# Revit family: ConcealedCistern-ForWallHungWCPans-8cm-WithAdjustableThinMetalFeet-VitrA-768-1851
name_source: partatom
category: Plumbing Fixtures
revit_build: Autodesk Revit 2017 (Build: 20160225_1515(x64)
units: mm (PartAtom-declared; Revit-internal decimal feet)

## family parameters
Cut with Voids When Loaded = No
Host = Face
OmniClass Number = 23.45.00.00
OmniClass Title = Sanitary, Laundry, and Cleaning Equipment
Part Type = Normal
Room Calculation Point = No
Round Connector Dimension = Use Diameter
Shared = Yes

## types (2) — shared parameters
BIMobject category = Toilet Cisterns
Brand = Vitra
CW Connection = Yes
Coating Material = Console
Default Elevation = 1000 mm  [stored 3.28084 ft]
Design country = Turkey
HW Connection = No
IFC Classification = Sanitary Terminal
Manufacturer = Vitra
Manufacturer name = Vitra
Mounting type = Assembly to floor
NBS Referans Code = 35-93-90
NBS Referans Description = Wc Cisterns
Nominal Depth (mm) = 80 mm  [stored 0.262467 ft]
Nominal Height (mm) = 1100 mm
Nominal Width (mm) = 500 mm  [stored 1.64042 ft]
OmniClass Code = 23-31 19 19
OmniClass Description = Water Closets
Outlet Angle = 45.00°
Primary Material = Orange
Product Type = Concealed Cistern
Product certification = https://www.vitraglobal.com
Product family = Vitra
Product group = Concealed Cistern for Wall-Hung WC Pans
Product url = https://www.vitra.com.tr
Secondary Material = White
Technical description = https://www.vitra.com.tr
Third Material = Blue
URL = https://www.vitra.com.tr
Uniclass 2.0 Code = PR-35-93-90
Uniclass 2.0 Description = Wc Cisterns
Uniclass 2015 Code = Pr_40_20_93_89
Uniclass 2015 Name = WC cisterns
Vent Connection = No
Warranty Period (Year) = 10 Years
Waste Connection = Yes
Weight Net (kg) = 8
Youtube = https://www.youtube.com

## per-type parameters (varying)
| type | Article No. (default) | Description | Model | Product Properties | Product SKU |
| ConcealedCistern-ForWallHungWCPans-3/6lt-WithAdjustableThickMetalFeet-8cm-FloorMounting-VitrA-768-1851-01 | 768-1851-01 | VitrA Concealed Cistern for Wall-Hung WC Pans
Standart Installation Set - Adjusted to 3/6lt - 8 cm | 768-1851-01 | Concealed Cistern for Wall-Hung WC Pans
Standart Installation Set - Adjusted to 3/6lt 8 cm | 768-1851-01 |
| ConcealedCistern-ForWallHungWCPans-2.5/4lt-WithAdjustableThickMetalFeet-8cm-FloorMounting-VitrA-768-1851-02 | 768-1851-02 | VitrA Concealed Cistern for Wall-Hung WC Pans
Standart Installation Set - Adjusted to 2.5/4lt - 8 cm | 768-1851-02 | Concealed Cistern for Wall-Hung WC Pans
Standart Installation Set - Adjusted to 2.5/4lt - 8cm | 768-1851-02 |

note: [stored X ft] marks values corroborated as IEEE doubles in the binary element streams (Revit-internal decimal feet)

## geometry (parser evidence)
native form markers: Sweep x1
no freeform markers — native parametric forms only
